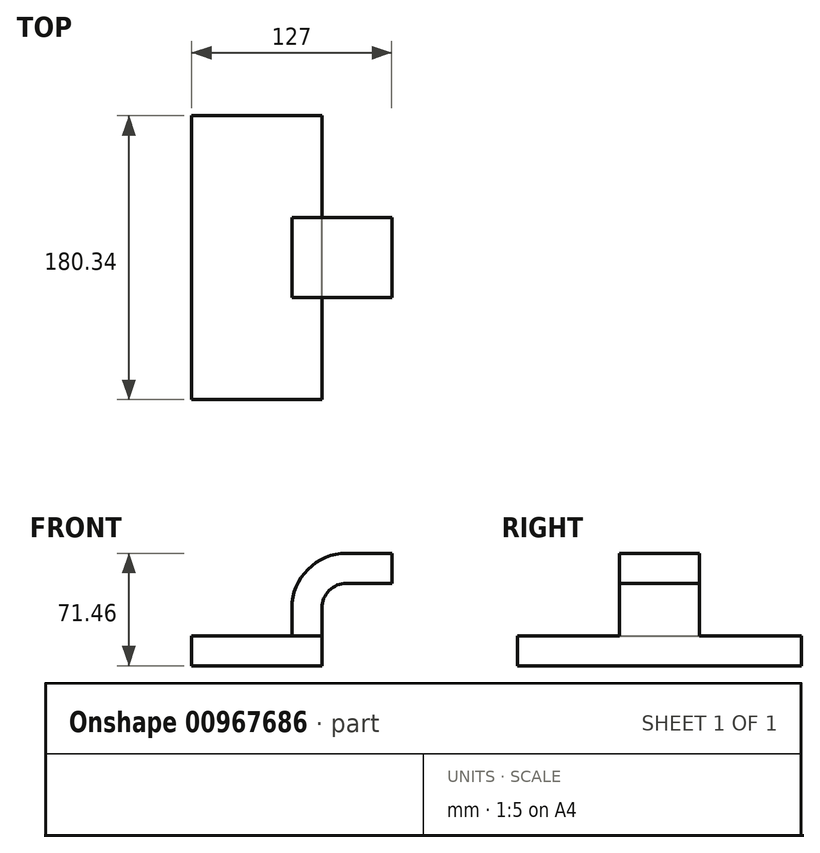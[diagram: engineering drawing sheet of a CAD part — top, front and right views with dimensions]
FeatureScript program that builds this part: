
annotation { "Feature Type Name" : "Feature", "Feature Type Description" : "" }
export const myFeature = defineFeature(function(context is Context, id is Id, definition is map)
    precondition{}
    {
        {
            var Q0;
            Q0=qCreatedBy(makeId("Front.planeOp"),FACE);
            var sketch = newSketch(context, id + "F0", { "sketchPlane" : qUnion([Q0])});
            skLineSegment(sketch, "E0.bottom", {"start": v(41.27, 9.53) * mm, "end": v(-41.28, 9.53) * mm});
            skLineSegment(sketch, "E0.top", {"start": v(41.28, -9.52) * mm, "end": v(-41.27, -9.52) * mm});
            skLineSegment(sketch, "E0.left", {"start": v(41.28, 9.53) * mm, "end": v(41.28, -9.52) * mm});
            skLineSegment(sketch, "E0.right", {"start": v(-41.28, 9.53) * mm, "end": v(-41.27, -9.52) * mm});
            skPoint(sketch, "E0.middle", {"position": v(0, 0) * mm});
            skLineSegment(sketch, "E1.bottom", {"start": v(111.12, 66.68) * mm, "end": v(60.32, 66.68) * mm});
            skLineSegment(sketch, "E1.top", {"start": v(111.12, 38.1) * mm, "end": v(60.32, 38.1) * mm});
            skLineSegment(sketch, "E1.left", {"start": v(111.12, 66.68) * mm, "end": v(111.12, 38.1) * mm});
            skLineSegment(sketch, "E1.right", {"start": v(60.32, 66.68) * mm, "end": v(60.32, 38.1) * mm});
            skPoint(sketch, "E1.middle", {"position": v(85.72, 52.39) * mm});
            skLineSegment(sketch, "E2", {"start": v(41.27, 9.53) * mm, "end": v(41.27, 27) * mm});
            skArc(sketch, "E3", {"start": v(41.27, 27) * mm, "mid": v(45.92, 38.23) * mm, "end": v(57.15, 42.88) * mm});
            skLineSegment(sketch, "E4", {"start": v(57.15, 42.88) * mm, "end": v(85.72, 42.88) * mm});
            skLineSegment(sketch, "E5.0", {"start": v(57.15, 61.93) * mm, "end": v(85.72, 61.93) * mm});
            skArc(sketch, "E5.1", {"start": v(22.23, 27) * mm, "mid": v(32.45, 51.7) * mm, "end": v(57.15, 61.93) * mm});
            skLineSegment(sketch, "E5.2", {"start": v(22.22, 9.53) * mm, "end": v(22.22, 27) * mm});
            skLineSegment(sketch, "E6", {"start": v(85.72, 38.1) * mm, "end": v(85.72, 66.68) * mm});
            skFitSpline(sketch, "E7", {"points": [v(-41.28, 9.53) * mm, v(57.15, 61.93) * mm], "startDerivative": vector(16.37, 56.53) * mm, "endDerivative": vector(158.63, -9.33) * mm});
            skSolve(sketch);
        }
        {
            var Q0;
            Q0=makeQuery(id+"F0.imprint","IMPRINT",FACE,{"disambiguationData":[TD([[makeQuery(id+"F0.imprint","IMPRINT",EDGE,{"derivedFrom":sQuery(id+"F0.wireOp",EDGE,"E0.top")}),-1.0]])]});
            extrude(context, id + "F1", {"entities" : qUnion([Q0]), "endBound" : BoundingType.SYMMETRIC, "depth" : 180.34 * mm, "offsetDistance" : 25.4 * mm});
        }
        {
            var Q0;
            {var subQ1=sQuery(id+"F0.wireOp",EDGE,"E2");Q0=makeQuery(id+"F0.imprint","IMPRINT",FACE,{"disambiguationData":[TD([[makeQuery(id+"F0.imprint","IMPRINT",EDGE,{"derivedFrom":subQ1}),1.0]])]});}
            var Q1;
            {var subQ0=sQuery(id+"F0.wireOp",EDGE,"E5.0");var subQ1=sQuery(id+"F0.wireOp",EDGE,"E1.right");var subQ2=makeQuery(id+"F0.imprint","INTERSECT",VERTEX,{"derivedFrom":[subQ1,subQ0]});Q1=makeQuery(id+"F0.imprint","IMPRINT",FACE,{"disambiguationData":[TD([[makeQuery(id+"F0.imprint","IMPRINT",EDGE,{"disambiguationData":[TD([[subQ2,-1.0]])],"derivedFrom":subQ1}),1.0]])]});}
            extrude(context, id + "F2", {"entities" : qUnion([Q0, Q1]), "operationType" : NewBodyOperationType.ADD, "endBound" : BoundingType.SYMMETRIC, "depth" : 50.8 * mm, "offsetDistance" : 25.4 * mm});
        }
        {
            var Q0;
            Q0=makeQuery(id+"F0.imprint","IMPRINT",FACE,{"disambiguationData":[TD([[makeQuery(id+"F0.imprint","IMPRINT",EDGE,{"derivedFrom":sQuery(id+"F0.wireOp",EDGE,"E5.1")}),1.0]])]});
            extrude(context, id + "F3", {"entities" : qUnion([Q0]), "operationType" : NewBodyOperationType.ADD, "endBound" : BoundingType.SYMMETRIC, "depth" : 15.88 * mm, "offsetDistance" : 25.4 * mm});
        }
    });
